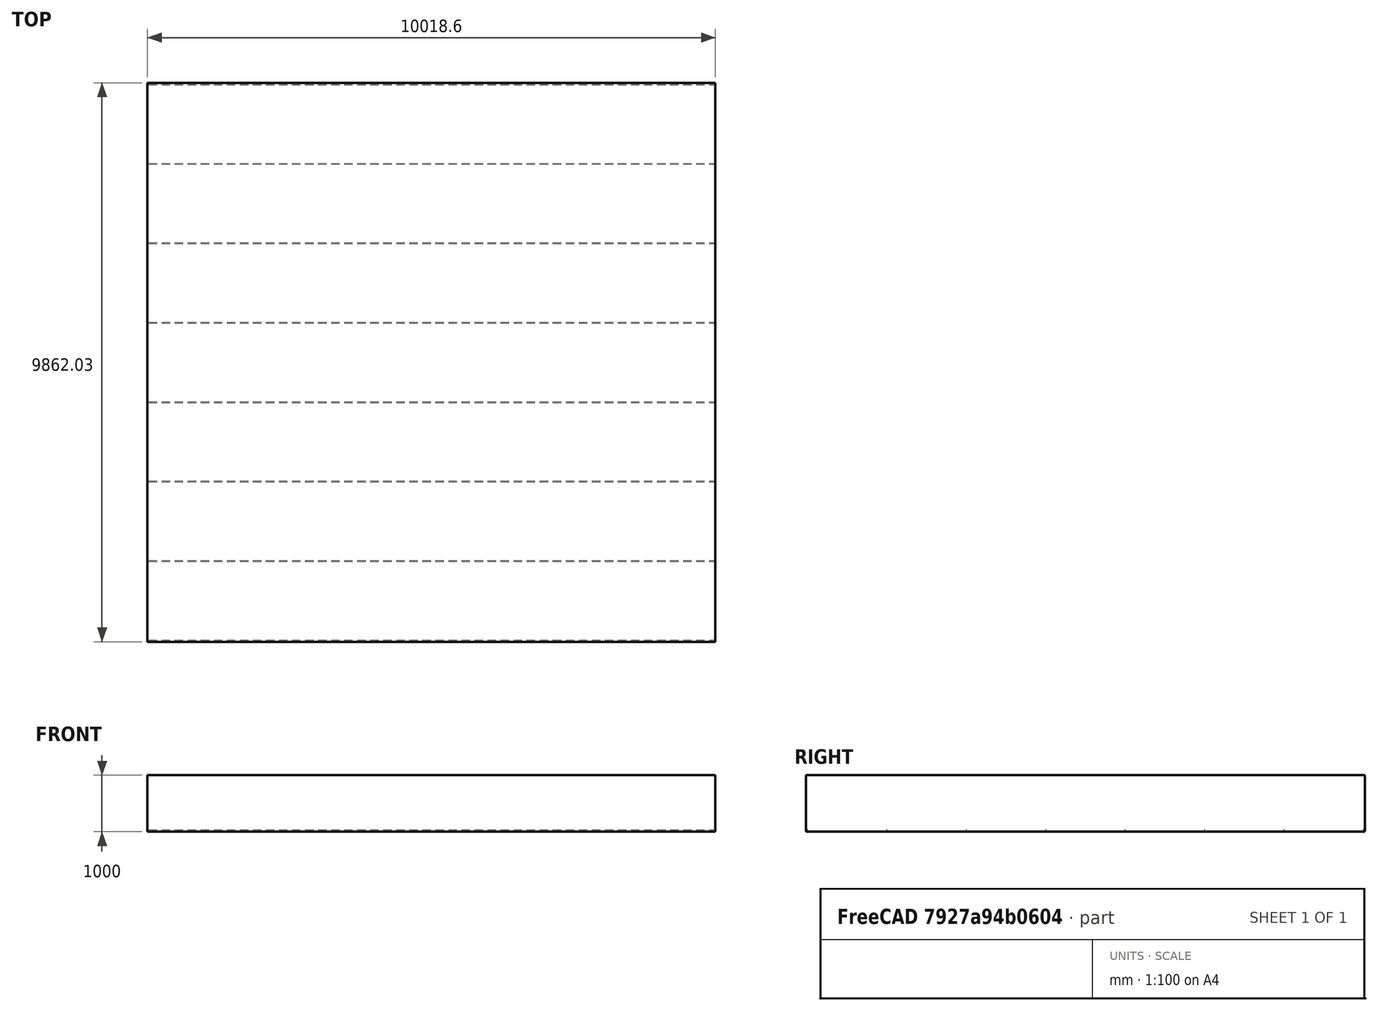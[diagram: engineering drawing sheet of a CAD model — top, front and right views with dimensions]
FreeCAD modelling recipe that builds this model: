
FCSTD DOCUMENT  (FreeCAD 0.19R24267 +99 (Git))
Label: SLAB WITH REINFORCEMENT
License: All rights reserved
LicenseURL: http://en.wikipedia.org/wiki/All_rights_reserved
objects: Part::FeaturePython×2, Part::Part2DObjectPython×1, Sketcher::SketchObject×1
note: 4 computed .brp shape members not serialized (recipe doc carries the construction recipe); baked Part::Feature solids carry a one-line shape summary decoded from their .brp

FEATURE [Part::Part2DObjectPython] Rectangle001  # Draft 2D object (typed FeaturePython)
  Area = 9.88034e+07
  ChamferSize = 0
  Columns = 1
  FilletRadius = 0
  Height = 9862.03
  Length = 10018.6
  MakeFace = true
  Placement = pos=(-9919.94,91.114,0) rot=(0,0,1;0rad)
  Rows = 1
FEATURE [Part::FeaturePython] Structure  # Arch/BIM 172 (typed FeaturePython)
  Base = -> Rectangle001
  FaceMaker = 0
  Height = 1000
  HorizontalArea = 9.88034e+07
  IfcData = attributes={"GlobalId": {"name": "GlobalId", "type": "IfcGloballyUniqueId", "is_enum": false, "enum_values": []}, "Description": {"... (+484 chars omitted),+1 more (map truncated)
  IfcType = 172
  Length = 0
  MoveBase = false
  MoveWithHost = false
  Nodes = (2) [(-4910.66,5022.13,0),(-4910.66,5022.13,1000)]
  NodesOffset = 0
  Normal = (0,0,0)
  PerimeterLength = 39761.2
  PredefinedType = 0
  VerticalArea = 3.97612e+07
  Width = 100
FEATURE [Sketcher::SketchObject] Sketch
  FullyConstrained = false
  MapMode = 5
  Placement = pos=(0,91.114,0) rot=(1,0,0;1.5708rad)
  Support = -> [Structure]
  sketch-geometry (1):
    g0: LineSegment StartX=-9899.94 StartY=26 StartZ=0 EndX=78.6247 EndY=26 EndZ=0
FEATURE [Part::FeaturePython] Rebar  label="StraightRebar"  # Arch/BIM 110 (typed FeaturePython)
  Amount = 8
  AmountCheck = true
  Base = -> Sketch
  Cover = 20
  CoverAlong = Bottom Side
  Diameter = 12
  Direction = (0,0,0)
  Distance = 0
  FrontCover = 20
  HorizontalArea = 0
  Host = -> Structure
  IfcType = 110
  LeftBottomCover = 20
  Length = 9978.57
  Mark = StraightRebar
  MoveBase = false
  MoveWithHost = false
  OffsetEnd = 26
  OffsetStart = 26
  Orientation = Horizontal
  PerimeterLength = 0
  PlacementList = 8 placements: arithmetic series from (0,26,-5.77316e-15) step (0,1401.43,-3.1118e-13) to (0,9836.03,-2.18404e-12)
  RebarShape = 0
  RightTopCover = 20
  Rounding = 0
  Spacing = 1401.43
  TotalLength = 79828.5
  TrueSpacing = 8
  VerticalArea = 0
